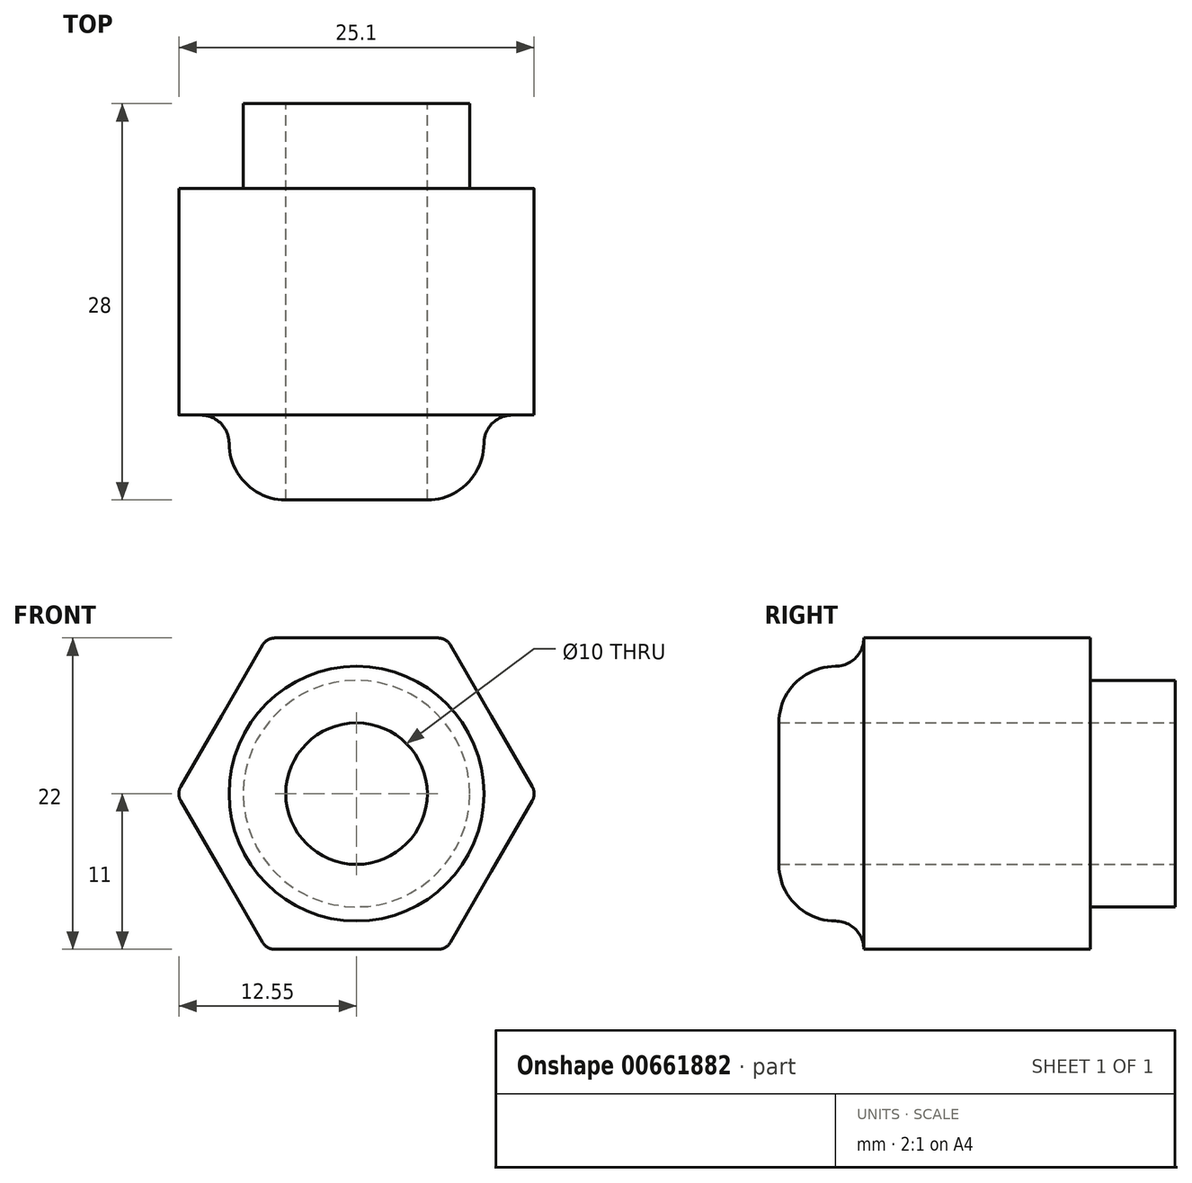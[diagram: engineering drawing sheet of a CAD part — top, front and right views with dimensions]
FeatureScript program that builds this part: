
annotation { "Feature Type Name" : "Feature", "Feature Type Description" : "" }
export const myFeature = defineFeature(function(context is Context, id is Id, definition is map)
    precondition{}
    {
        {
            var Q0;
            Q0=qCreatedBy(makeId("Front.planeOp"),FACE);
            var sketch = newSketch(context, id + "F0", { "sketchPlane" : qUnion([Q0])});
            skCircle(sketch, "E0.cCircle", {"center": v(0, 0) * mm, "radius": 11 * mm, "construction": true});
            skLineSegment(sketch, "E0.0", {"start": v(-6.35, 11) * mm, "end": v(6.35, 11) * mm});
            skLineSegment(sketch, "E0.1", {"start": v(6.35, 11) * mm, "end": v(12.7, 0) * mm});
            skLineSegment(sketch, "E0.2", {"start": v(12.7, 0) * mm, "end": v(6.35, -11) * mm});
            skLineSegment(sketch, "E0.3", {"start": v(6.35, -11) * mm, "end": v(-6.35, -11) * mm});
            skLineSegment(sketch, "E0.4", {"start": v(-6.35, -11) * mm, "end": v(-12.7, 0) * mm});
            skLineSegment(sketch, "E0.5", {"start": v(-12.7, 0) * mm, "end": v(-6.35, 11) * mm});
            skPoint(sketch, "E0.0.midPoint", {"position": v(0, 11) * mm});
            skCircle(sketch, "E1", {"center": v(0, 0) * mm, "radius": 5 * mm});
            skSolve(sketch);
        }
        {
            var Q0;
            Q0=qCreatedBy(makeId("Right.planeOp"),FACE);
            var sketch = newSketch(context, id + "F1", { "sketchPlane" : qUnion([Q0])});
            skLineSegment(sketch, "E2", {"start": v(0, 0) * mm, "end": v(-48.65, 0) * mm, "construction": true});
            skLineSegment(sketch, "E3", {"start": v(0, 9) * mm, "end": v(-18, 9) * mm});
            skLineSegment(sketch, "E4", {"start": v(0, 5) * mm, "end": v(-22, 5) * mm});
            skArc(sketch, "E5", {"start": v(-18, 9) * mm, "mid": v(-20.83, 7.83) * mm, "end": v(-22, 5) * mm});
            skLineSegment(sketch, "E6", {"start": v(-22, 5) * mm, "end": v(-22, 0) * mm, "construction": true});
            skLineSegment(sketch, "E7", {"start": v(0, 9) * mm, "end": v(0, 8) * mm});
            skLineSegment(sketch, "E8", {"start": v(-18, 9) * mm, "end": v(-18, 5) * mm, "construction": true});
            skLineSegment(sketch, "E9", {"start": v(0, 5) * mm, "end": v(6, 5) * mm});
            skLineSegment(sketch, "E10", {"start": v(6, 5) * mm, "end": v(6, 8) * mm});
            skLineSegment(sketch, "E11", {"start": v(6, 8) * mm, "end": v(0, 8) * mm});
            skSolve(sketch);
        }
        {
            var Q0;
            Q0 = qSketchRegion(id + "F1", true);
            var Q1;
            Q1=sQuery(id+"F1.wireOp",EDGE,"E2");
            revolve(context, id + "F2", {"surfaceOperationType" : NewSurfaceOperationType.NEW, "entities" : qUnion([Q0]), "axis" : qUnion([Q1]), "revolveType" : RevolveType.FULL});
        }
        {
            var Q0;
            Q0=makeQuery(id+"F0.imprint","IMPRINT",FACE,{"disambiguationData":[TD([[makeQuery(id+"F0.imprint","IMPRINT",EDGE,{"derivedFrom":sQuery(id+"F0.wireOp",EDGE,"E0.0")}),-1.0]])]});
            extrude(context, id + "F3", {"entities" : qUnion([Q0]), "operationType" : NewBodyOperationType.ADD, "depth" : 16 * mm, "offsetDistance" : 25 * mm});
        }
        {
            var Q0;
            Q0=makeQuery(id+"F3.boolean.opBoolean","INTERSECT",EDGE,{"derivedFrom":[makeQuery(id+"F2.opRevolve","SWEPT_FACE",FACE,{"disambiguationData":[OSD([sQuery(id+"F1.wireOp",EDGE,"E3")])]}),makeQuery(id+"F3.opExtrude","CAP_FACE",FACE,{"disambiguationData":[OSD([sQuery(id+"F0.wireOp",EDGE,"E0.0"),sQuery(id+"F0.wireOp",EDGE,"E0.1"),sQuery(id+"F0.wireOp",EDGE,"E0.2"),sQuery(id+"F0.wireOp",EDGE,"E0.3"),sQuery(id+"F0.wireOp",EDGE,"E0.4"),sQuery(id+"F0.wireOp",EDGE,"E0.5"),sQuery(id+"F0.wireOp",EDGE,"E1")])],"isStart":false})]});
            fillet(context, id + "F4", {"entities" : qUnion([Q0]), "radius" : 2 * mm, "tangentPropagation" : true, "allowEdgeOverflow" : false});
        }
        {
            var Q0;
            Q0=makeQuery(id+"F3.opExtrude","SWEPT_EDGE",EDGE,{"disambiguationData":[OSD([sQuery(id+"F0.wireOp",EDGE,"E0.0"),sQuery(id+"F0.wireOp",EDGE,"E0.5")])]});
            var Q1;
            Q1=makeQuery(id+"F3.opExtrude","SWEPT_EDGE",EDGE,{"disambiguationData":[OSD([sQuery(id+"F0.wireOp",EDGE,"E0.4"),sQuery(id+"F0.wireOp",EDGE,"E0.5")])]});
            var Q2;
            Q2=makeQuery(id+"F3.opExtrude","SWEPT_EDGE",EDGE,{"disambiguationData":[OSD([sQuery(id+"F0.wireOp",EDGE,"E0.3"),sQuery(id+"F0.wireOp",EDGE,"E0.4")])]});
            var Q3;
            Q3=makeQuery(id+"F3.opExtrude","SWEPT_EDGE",EDGE,{"disambiguationData":[OSD([sQuery(id+"F0.wireOp",EDGE,"E0.2"),sQuery(id+"F0.wireOp",EDGE,"E0.3")])]});
            var Q4;
            Q4=makeQuery(id+"F3.opExtrude","SWEPT_EDGE",EDGE,{"disambiguationData":[OSD([sQuery(id+"F0.wireOp",EDGE,"E0.1"),sQuery(id+"F0.wireOp",EDGE,"E0.2")])]});
            var Q5;
            Q5=makeQuery(id+"F3.opExtrude","SWEPT_EDGE",EDGE,{"disambiguationData":[OSD([sQuery(id+"F0.wireOp",EDGE,"E0.0"),sQuery(id+"F0.wireOp",EDGE,"E0.1")])]});
            fillet(context, id + "F5", {"entities" : qUnion([Q0, Q1, Q2, Q3, Q4, Q5]), "radius" : 1 * mm, "tangentPropagation" : true, "allowEdgeOverflow" : false});
        }
    });
